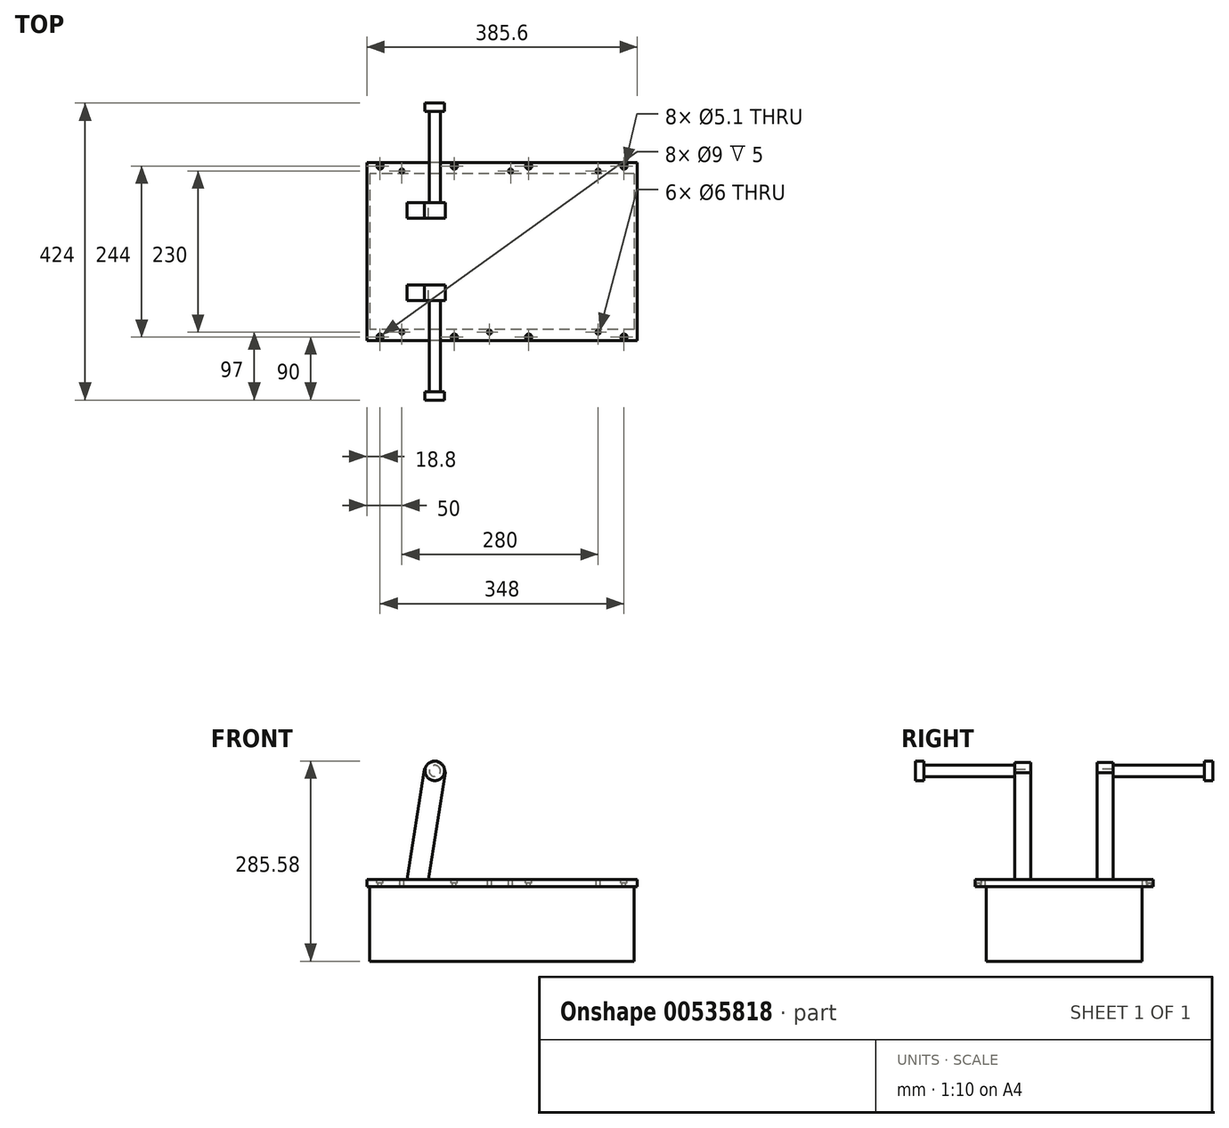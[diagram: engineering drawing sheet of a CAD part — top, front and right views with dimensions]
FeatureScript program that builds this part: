
annotation { "Feature Type Name" : "Feature", "Feature Type Description" : "" }
export const myFeature = defineFeature(function(context is Context, id is Id, definition is map)
    precondition{}
    {
        {
            var Q0;
            Q0=qCreatedBy(makeId("Top.planeOp"),FACE);
            var sketch = newSketch(context, id + "F0", { "sketchPlane" : qUnion([Q0])});
            skLineSegment(sketch, "E0.bottom", {"start": v(192.8, -127) * mm, "end": v(-192.8, -127) * mm});
            skLineSegment(sketch, "E0.top", {"start": v(192.8, 127) * mm, "end": v(-192.8, 127) * mm});
            skLineSegment(sketch, "E0.left", {"start": v(192.8, -127) * mm, "end": v(192.8, 127) * mm});
            skLineSegment(sketch, "E0.right", {"start": v(-192.8, -127) * mm, "end": v(-192.8, 127) * mm});
            skPoint(sketch, "E0.middle", {"position": v(0, 0) * mm});
            skSolve(sketch);
        }
        {
            var Q0;
            Q0=qSketchRegion(id+"F0",true);
            extrude(context, id + "F1", {"entities" : qUnion([Q0]), "depth" : 10 * mm});
        }
        {
            var Q0;
            Q0=makeQuery(id+"F1.opExtrude","CAP_FACE",FACE,{"disambiguationData":[OSD([sQuery(id+"F0.wireOp",EDGE,"E0.bottom"),sQuery(id+"F0.wireOp",EDGE,"E0.top"),sQuery(id+"F0.wireOp",EDGE,"E0.left"),sQuery(id+"F0.wireOp",EDGE,"E0.right")])],"isStart":true});
            var sketch = newSketch(context, id + "F2", { "sketchPlane" : qUnion([Q0])});
            skLineSegment(sketch, "E1.bottom", {"start": v(188.5, -111.15) * mm, "end": v(-188.5, -111.15) * mm});
            skLineSegment(sketch, "E1.top", {"start": v(188.5, 111.15) * mm, "end": v(-188.5, 111.15) * mm});
            skLineSegment(sketch, "E1.left", {"start": v(188.5, -111.15) * mm, "end": v(188.5, 111.15) * mm});
            skLineSegment(sketch, "E1.right", {"start": v(-188.5, -111.15) * mm, "end": v(-188.5, 111.15) * mm});
            skPoint(sketch, "E1.middle", {"position": v(0, 0) * mm});
            skSolve(sketch);
        }
        {
            var Q0;
            Q0=qSketchRegion(id+"F2",true);
            extrude(context, id + "F3", {"entities" : qUnion([Q0]), "operationType" : NewBodyOperationType.ADD, "depth" : 106.5 * mm});
        }
        {
            var Q0;
            {var subQ0=sQuery(id+"F0.wireOp",EDGE,"E0.left");var subQ1=sQuery(id+"F0.wireOp",EDGE,"E0.top");var subQ2=sQuery(id+"F0.wireOp",EDGE,"E0.right");var subQ3=sQuery(id+"F0.wireOp",EDGE,"E0.bottom");Q0=makeQuery(id+"FRL6UhUfdcv4TXD_1.boolean.opBoolean","SPLIT",FACE,{"disambiguationData":[TD([makeQuery(id+"F1.opExtrude","SWEPT_FACE",FACE,{"disambiguationData":[OSD([subQ3])]})])],"derivedFrom":makeQuery(id+"F1.opExtrude","CAP_FACE",FACE,{"disambiguationData":[OSD([subQ3,subQ1,subQ0,subQ2])],"isStart":false})});}
            var sketch = newSketch(context, id + "F4", { "sketchPlane" : qUnion([Q0])});
            skPoint(sketch, "E2", {"position": v(-142.8, 115) * mm});
            skPoint(sketch, "E3", {"position": v(12.2, 115) * mm});
            skPoint(sketch, "E4", {"position": v(137.2, 115) * mm});
            skPoint(sketch, "E5.MirrorP", {"position": v(137.2, -115) * mm});
            skPoint(sketch, "E6.MirrorP", {"position": v(-142.8, -115) * mm});
            skPoint(sketch, "E7", {"position": v(-17.8, -115) * mm});
            skPoint(sketch, "E8", {"position": v(-174, 122) * mm});
            skPoint(sketch, "E9", {"position": v(-68, 122) * mm});
            skPoint(sketch, "E10", {"position": v(38, 122) * mm});
            skPoint(sketch, "E11", {"position": v(174, 122) * mm});
            skPoint(sketch, "E12.MirrorP", {"position": v(174, -122) * mm});
            skPoint(sketch, "E13.MirrorP", {"position": v(38, -122) * mm});
            skPoint(sketch, "E14.MirrorP", {"position": v(-68, -122) * mm});
            skPoint(sketch, "E15.MirrorP", {"position": v(-174, -122) * mm});
            skSolve(sketch);
        }
        {
            var Q0;
            Q0=sQuery(id+"F4.wireOp",VERTEX,"E2");
            var Q1;
            Q1=sQuery(id+"F4.wireOp",VERTEX,"E3");
            var Q2;
            Q2=sQuery(id+"F4.wireOp",VERTEX,"E4");
            var Q3;
            Q3=sQuery(id+"F4.wireOp",VERTEX,"E5.MirrorP");
            var Q4;
            Q4=sQuery(id+"F4.wireOp",VERTEX,"E7");
            var Q5;
            Q5=sQuery(id+"F4.wireOp",VERTEX,"E6.MirrorP");
            var Q6;
            Q6=makeQuery(id+"F1.opExtrude","SWEPT_BODY",BODY,{"disambiguationData":[OSD([sQuery(id+"F0.wireOp",EDGE,"E0.bottom"),sQuery(id+"F0.wireOp",EDGE,"E0.top"),sQuery(id+"F0.wireOp",EDGE,"E0.left"),sQuery(id+"F0.wireOp",EDGE,"E0.right")])]});
            hole(context, id + "F5", {"style" : HoleStyle.SIMPLE, "endStyle" : HoleEndStyle.BLIND, "holeDiameter" : 6 * mm, "holeDepth" : 10 * mm, "tappedDepth" : 12 * mm, "tapClearance" : 3, "locations" : qUnion([Q0, Q1, Q2, Q3, Q4, Q5]), "scope" : qUnion([Q6])});
        }
        {
            var Q0;
            Q0=sQuery(id+"F4.wireOp",VERTEX,"E8");
            var Q1;
            Q1=sQuery(id+"F4.wireOp",VERTEX,"E9");
            var Q2;
            Q2=sQuery(id+"F4.wireOp",VERTEX,"E10");
            var Q3;
            Q3=sQuery(id+"F4.wireOp",VERTEX,"E11");
            var Q4;
            Q4=sQuery(id+"F4.wireOp",VERTEX,"E12.MirrorP");
            var Q5;
            Q5=sQuery(id+"F4.wireOp",VERTEX,"E13.MirrorP");
            var Q6;
            Q6=sQuery(id+"F4.wireOp",VERTEX,"E14.MirrorP");
            var Q7;
            Q7=sQuery(id+"F4.wireOp",VERTEX,"E15.MirrorP");
            var Q8;
            Q8=makeQuery(id+"F1.opExtrude","SWEPT_BODY",BODY,{"disambiguationData":[OSD([sQuery(id+"F0.wireOp",EDGE,"E0.bottom"),sQuery(id+"F0.wireOp",EDGE,"E0.top"),sQuery(id+"F0.wireOp",EDGE,"E0.left"),sQuery(id+"F0.wireOp",EDGE,"E0.right")])]});
            hole(context, id + "F6", {"style" : HoleStyle.C_BORE, "endStyle" : HoleEndStyle.BLIND, "holeDiameter" : 5.1 * mm, "cBoreDiameter" : 9 * mm, "cBoreDepth" : 5 * mm, "holeDepth" : 10 * mm, "tappedDepth" : 12 * mm, "tapClearance" : 3, "locations" : qUnion([Q0, Q1, Q2, Q3, Q4, Q5, Q6, Q7]), "scope" : qUnion([Q8])});
        }
        {
            var Q0;
            Q0=qCreatedBy(makeId("Front.planeOp"),FACE);
            cPlane(context, id + "F7", {"entities" : qUnion([Q0]), "cplaneType" : CPlaneType.OFFSET, "offset" : 47.45 * mm, "width" : 150 * mm, "height" : 150 * mm});
        }
        {
            var Q0;
            Q0=qCreatedBy(id+"F7.planeOp",FACE);
            var sketch = newSketch(context, id + "F8", { "sketchPlane" : qUnion([Q0])});
            skLineSegment(sketch, "E16", {"start": v(-95.82, 165.08) * mm, "end": v(-126.53, -28.83) * mm, "construction": true});
            skLineSegment(sketch, "E17", {"start": v(-110.63, 167.43) * mm, "end": v(-139.9, -17.39) * mm});
            skLineSegment(sketch, "E18", {"start": v(-81, 162.73) * mm, "end": v(-110.27, -22.08) * mm});
            skLineSegment(sketch, "E19", {"start": v(-110.63, 167.43) * mm, "end": v(-81, 162.73) * mm, "construction": true});
            skArc(sketch, "E20", {"start": v(-81, 162.73) * mm, "mid": v(-93.98, 176.7) * mm, "end": v(-110.63, 167.43) * mm});
            skLineSegment(sketch, "E21", {"start": v(-139.9, -17.39) * mm, "end": v(-110.27, -22.08) * mm});
            skCircle(sketch, "E22", {"center": v(-95.82, 165.08) * mm, "radius": 8 * mm, "construction": true});
            skSolve(sketch);
        }
        {
            var Q0;
            Q0=qSketchRegion(id+"F8",true);
            extrude(context, id + "F9", {"entities" : qUnion([Q0]), "depth" : 22.55 * mm});
        }
        {
            var Q0;
            Q0=makeQuery(id+"F8.imprint","IMPRINT",FACE,{"disambiguationData":[TD([[makeQuery(id+"F8.imprint","IMPRINT",EDGE,{"derivedFrom":sQuery(id+"F8.wireOp",EDGE,"E17")}),1.0]])]});
            var sketch = newSketch(context, id + "F10", { "sketchPlane" : qUnion([Q0])});
            skCircle(sketch, "E23", {"center": v(-95.82, 165.08) * mm, "radius": 8 * mm});
            skSolve(sketch);
        }
        {
            var Q0;
            Q0=qSketchRegion(id+"F10",true);
            extrude(context, id + "F11", {"entities" : qUnion([Q0]), "operationType" : NewBodyOperationType.ADD, "depth" : 164.55 * mm});
        }
        {
            var Q0;
            Q0=makeQuery(id+"F11.opExtrude","CAP_FACE",FACE,{"disambiguationData":[OSD([sQuery(id+"F10.wireOp",EDGE,"E23")])],"isStart":false});
            var sketch = newSketch(context, id + "F12", { "sketchPlane" : qUnion([Q0])});
            skCircle(sketch, "E24", {"center": v(-95.82, 165.08) * mm, "radius": 14 * mm});
            skSolve(sketch);
        }
        {
            var Q0;
            Q0=qSketchRegion(id+"F12",true);
            extrude(context, id + "F13", {"entities" : qUnion([Q0]), "operationType" : NewBodyOperationType.ADD, "oppositeDirection" : true, "depth" : 12 * mm});
        }
        {
            var Q0;
            Q0=makeQuery(id+"F9.opExtrude","SWEPT_BODY",BODY,{"disambiguationData":[OSD([sQuery(id+"F8.wireOp",EDGE,"E17"),sQuery(id+"F8.wireOp",EDGE,"E18"),sQuery(id+"F8.wireOp",EDGE,"E20"),sQuery(id+"F8.wireOp",EDGE,"E21")])]});
            var Q1;
            Q1=qCreatedBy(makeId("Front.planeOp"),FACE);
            mirror(context, id + "F14", {"operationType" : NewBodyOperationType.ADD, "entities" : qUnion([Q0]), "mirrorPlane" : qUnion([Q1])});
        }
    });
